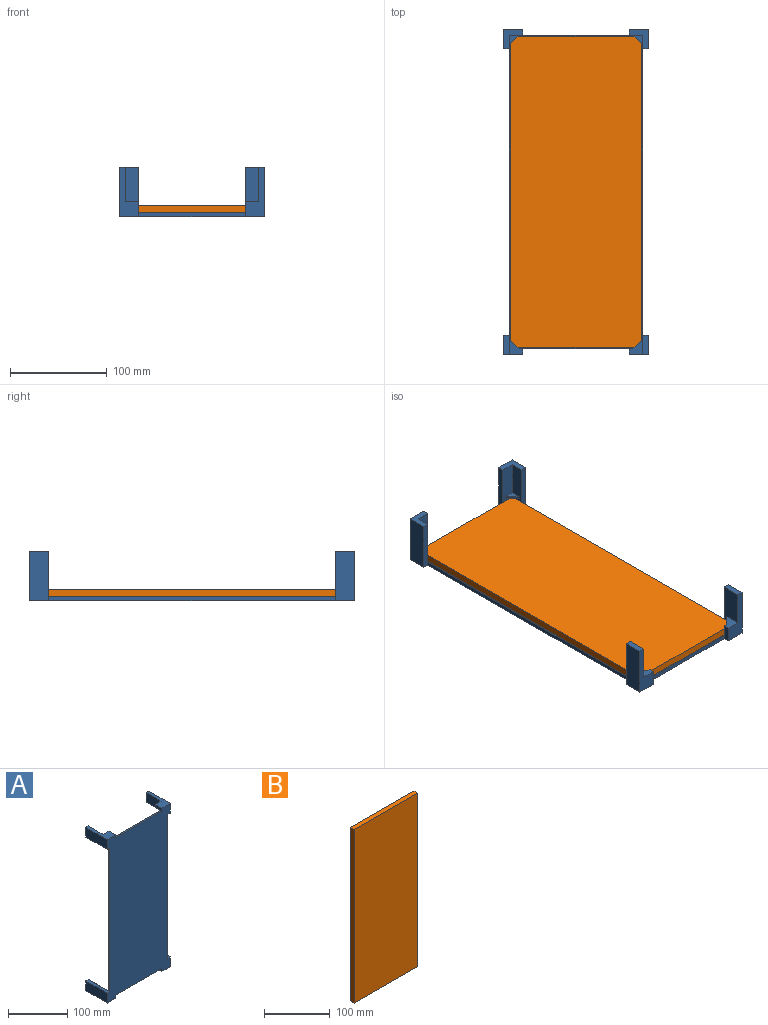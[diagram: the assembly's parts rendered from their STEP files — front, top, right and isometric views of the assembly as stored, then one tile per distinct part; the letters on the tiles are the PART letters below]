
ASSEMBLY  parts=2 mates=1
PART A: 46 faces, bbox 149.9x51.5x336.6 mm
  f0: plane 14x12mm, normal (0,0,-1), area 148mm2, adj f6,f8,f23,f43,f44,f45
  f1: plane 14x12mm, normal (0,0,-1), area 148mm2, adj f7,f9,f23,f40,f41,f42
  f2: plane 20x6mm, normal (0,1,0), area 120mm2, adj f5,f9,f14,f33
  f3: plane 51.48x20mm, normal (0,0,1), area 532.9mm2, adj f4,f6,f8,f16,f21,f45
  f4: plane 20x6mm, normal (0,1,0), area 120mm2, adj f3,f8,f21,f30
  f5: plane 51.48x20mm, normal (0,0,1), area 532.9mm2, adj f2,f7,f9,f14,f16,f42
  f6: plane 16x6mm, normal (1,0,0), area 96mm2, adj f0,f3,f16,f27,f45
  f7: plane 16x6mm, normal (-1,0,0), area 96mm2, adj f1,f5,f16,f27,f42
  f8: plane 47.48x20mm, normal (1,0,0), area 857.6mm2, adj f0,f3,f4,f23,f30,f43,f44,f45
  f9: plane 47.48x20mm, normal (-1,0,0), area 857.6mm2, adj f1,f2,f5,f23,f33,f40,f41,f42
  f10: plane 47.48x14mm, normal (0,0,1), area 644.7mm2, adj f11,f22,f23,f26,f37,f38,f39
  f11: plane 47.48x14mm, normal (-1,0,0), area 644.7mm2, adj f10,f22,f23,f32,f37,f38,f39
  f12: plane 47.48x14mm, normal (1,0,0), area 644.7mm2, adj f13,f15,f23,f29,f34,f35,f36
  f13: plane 47.48x14mm, normal (0,0,1), area 644.7mm2, adj f12,f15,f23,f25,f34,f35,f36
  f14: plane 51.48x20mm, normal (1,0,0), area 1029.6mm2, adj f2,f5,f16,f33
  f15: plane 20x20mm, normal (0,1,0), area 204mm2, adj f12,f13,f17,f20,f25,f29
  f16: plane 336.6x149.9mm, normal (0,-1,0), area 45578.3mm2, adj f3,f5,f6,f7,f14,f17,f18,f19
  f17: plane 51.48x20mm, normal (-1,0,0), area 1029.6mm2, adj f15,f16,f20,f29
  f18: plane 51.48x20mm, normal (0,0,-1), area 1029.6mm2, adj f16,f19,f22,f26
  f19: plane 51.48x20mm, normal (1,0,0), area 1029.6mm2, adj f16,f18,f22,f32
  f20: plane 51.48x20mm, normal (0,0,-1), area 1029.6mm2, adj f15,f16,f17,f25
  f21: plane 51.48x20mm, normal (-1,0,0), area 1029.6mm2, adj f3,f4,f16,f30
  f22: plane 20x20mm, normal (0,1,0), area 204mm2, adj f10,f11,f18,f19,f26,f32
  f23: plane 324.6x137.9mm, normal (0,1,0), area 44762.3mm2, adj f0,f1,f8,f9,f10,f11,f12,f13
  f24: plane 109.9x4mm, normal (0,0,-1), area 439.6mm2, adj f16,f23,f25,f26
  f25: plane 51.48x6mm, normal (1,0,0), area 308.9mm2, adj f13,f15,f16,f20,f24
  f26: plane 51.48x6mm, normal (-1,0,0), area 308.9mm2, adj f10,f16,f18,f22,f24
  f27: plane 109.9x4mm, normal (0,0,1), area 439.6mm2, adj f6,f7,f16,f23
  f28: plane 296.6x4mm, normal (-1,0,0), area 1186.4mm2, adj f16,f23,f29,f30
  f29: plane 51.48x6mm, normal (0,0,1), area 308.9mm2, adj f12,f15,f16,f17,f28
  f30: plane 51.48x6mm, normal (0,0,-1), area 308.9mm2, adj f4,f8,f16,f21,f28
  f31: plane 296.6x4mm, normal (1,0,0), area 1186.4mm2, adj f16,f23,f32,f33
  f32: plane 51.48x6mm, normal (0,0,1), area 308.9mm2, adj f11,f16,f19,f22,f31
  f33: plane 51.48x6mm, normal (0,0,-1), area 308.9mm2, adj f2,f9,f14,f16,f31
  f34: plane 10x10mm, normal (0.71,0,0.71), area 28.3mm2, adj f12,f13,f35,f36
  f35: plane 10x10mm, normal (0,-1,0), area 50mm2, adj f12,f13,f34
  f36: plane 10x10mm, normal (0,1,0), area 50mm2, adj f12,f13,f34
  f37: plane 10x10mm, normal (-0.71,0,0.71), area 28.3mm2, adj f10,f11,f38,f39
  f38: plane 10x10mm, normal (0,-1,0), area 50mm2, adj f10,f11,f37
  f39: plane 10x10mm, normal (0,1,0), area 50mm2, adj f10,f11,f37
  f40: plane 10x10mm, normal (-0.71,0,-0.71), area 28.3mm2, adj f1,f9,f41,f42
  f41: plane 10x10mm, normal (0,-1,0), area 50mm2, adj f1,f9,f40
  f42: plane 16x14mm, normal (0,1,0), area 134mm2, adj f1,f5,f7,f9,f40
  f43: plane 10x10mm, normal (0.71,0,-0.71), area 28.3mm2, adj f0,f8,f44,f45
  f44: plane 10x10mm, normal (0,-1,0), area 50mm2, adj f0,f8,f43
  f45: plane 16x14mm, normal (0,1,0), area 134mm2, adj f0,f3,f6,f8,f43
PART B: 6 faces, bbox 135.9x7.6x322.6 mm
  f0: plane 322.6x7.62mm, normal (1,0,0), area 2458.2mm2, adj f1,f3,f4,f5
  f1: plane 135.9x7.62mm, normal (0,0,-1), area 1035.6mm2, adj f0,f2,f4,f5
  f2: plane 322.6x7.62mm, normal (-1,0,0), area 2458.2mm2, adj f1,f3,f4,f5
  f3: plane 135.9x7.62mm, normal (0,0,1), area 1035.6mm2, adj f0,f2,f4,f5
  f4: plane 322.6x135.9mm, normal (0,1,0), area 43841.3mm2, adj f0,f1,f2,f3
  f5: plane 322.6x135.9mm, normal (0,-1,0), area 43841.3mm2, adj f0,f1,f2,f3
PLACE A rot(axis=(1,0,0),90deg) t=(0,0,4)mm
PLACE B rot(axis=(1,0,0),90deg) t=(0,0,4)mm
MATE fastened B.f5 <-> A.f23  axis (0,0,-1) through (0,0,4)mm
